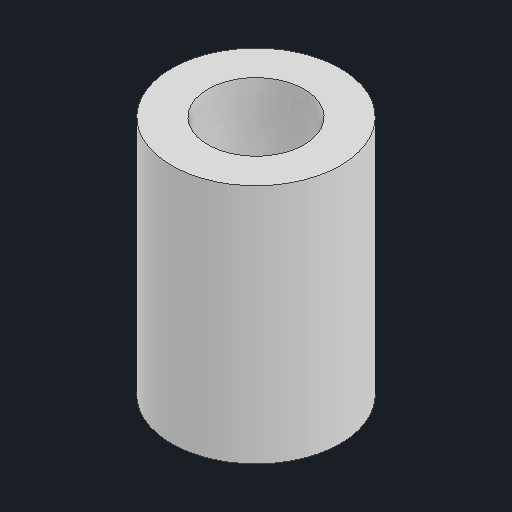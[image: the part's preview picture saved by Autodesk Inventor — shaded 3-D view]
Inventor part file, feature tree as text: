
AUTODESK INVENTOR PART (.ipt)
format: ipt  version: 2024 (Build 280153000, 153)  size: 88,064 bytes
history: native  units: in
note: dims shown in document units (in); Inventor stores cm internally (conversion verified against a paired STEP export)
features: other x3, sketch x1
ambient origin geometry x8: Origin, YZ Plane, XZ Plane, XY Plane, X Axis, Y Axis, Z Axis, Center Point
bodies: Solid1 (feature_tree)
feature tree (4):
  other  "10mm spacer.ipt"
  other  "Solid1::10mm spacer.ipt"
  other  "TaggingFeature1"
  sketch  "Sketch1"  dims[d0=0.3937in]
